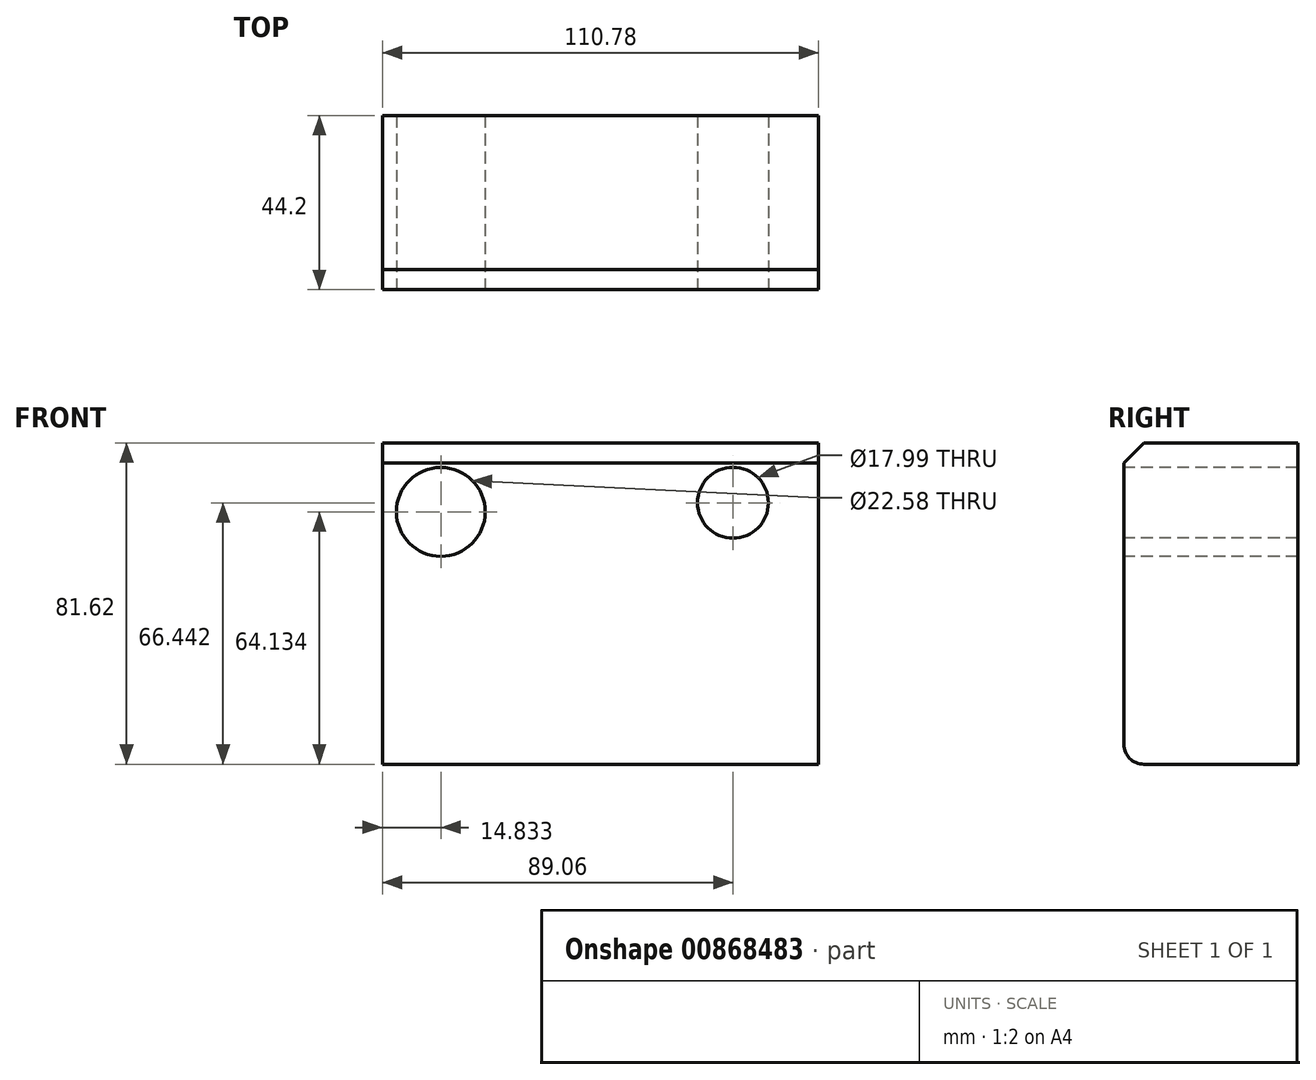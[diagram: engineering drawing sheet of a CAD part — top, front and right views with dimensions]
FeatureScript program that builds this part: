
annotation { "Feature Type Name" : "Feature", "Feature Type Description" : "" }
export const myFeature = defineFeature(function(context is Context, id is Id, definition is map)
    precondition{}
    {
        {
            var Q0;
            Q0=qCreatedBy(makeId("Front.planeOp"),FACE);
            var sketch = newSketch(context, id + "F0", { "sketchPlane" : qUnion([Q0])});
            skLineSegment(sketch, "E0.bottom", {"start": v(55.39, -40.8) * mm, "end": v(-55.39, -40.8) * mm});
            skLineSegment(sketch, "E0.top", {"start": v(55.39, 40.8) * mm, "end": v(-55.39, 40.8) * mm});
            skLineSegment(sketch, "E0.left", {"start": v(55.39, -40.8) * mm, "end": v(55.39, 40.8) * mm});
            skLineSegment(sketch, "E0.right", {"start": v(-55.39, -40.8) * mm, "end": v(-55.39, 40.8) * mm});
            skPoint(sketch, "E0.middle", {"position": v(0, 0) * mm});
            skSolve(sketch);
        }
        {
            var Q0;
            Q0=makeQuery(id+"F0.imprint","IMPRINT",FACE,{"disambiguationData":[TD([[makeQuery(id+"F0.imprint","IMPRINT",EDGE,{"derivedFrom":sQuery(id+"F0.wireOp",EDGE,"E0.bottom")}),-1.0]])]});
            extrude(context, id + "F1", {"entities" : qUnion([Q0]), "depth" : 44.2 * mm, "offsetDistance" : 25.4 * mm});
        }
        {
            var Q0;
            Q0=makeQuery(id+"F1.opExtrude","CAP_FACE",FACE,{"disambiguationData":[OSD([sQuery(id+"F0.wireOp",EDGE,"E0.bottom"),sQuery(id+"F0.wireOp",EDGE,"E0.top"),sQuery(id+"F0.wireOp",EDGE,"E0.left"),sQuery(id+"F0.wireOp",EDGE,"E0.right")])],"isStart":false});
            var sketch = newSketch(context, id + "F2", { "sketchPlane" : qUnion([Q0])});
            skCircle(sketch, "E1", {"center": v(-40.56, 23.32) * mm, "radius": 11.3 * mm});
            skCircle(sketch, "E2", {"center": v(33.67, 25.63) * mm, "radius": 9 * mm});
            skSolve(sketch);
        }
        {
            var Q0;
            Q0 = qSketchRegion(id + "F2", true);
            extrude(context, id + "F3", {"entities" : qUnion([Q0]), "operationType" : NewBodyOperationType.REMOVE, "endBound" : BoundingType.UP_TO_NEXT, "oppositeDirection" : true, "depth" : 25.4 * mm, "offsetDistance" : 25.4 * mm});
        }
        {
            var Q0;
            Q0=makeQuery(id+"F1.opExtrude","CAP_EDGE",EDGE,{"disambiguationData":[OSD([sQuery(id+"F0.wireOp",EDGE,"E0.top")])],"isStart":false});
            chamfer(context, id + "F4", {"entities" : qUnion([Q0]), "width" : 5.08 * mm, "tangentPropagation" : true});
        }
        {
            var Q0;
            Q0=makeQuery(id+"F1.opExtrude","CAP_EDGE",EDGE,{"disambiguationData":[OSD([sQuery(id+"F0.wireOp",EDGE,"E0.bottom")])],"isStart":false});
            fillet(context, id + "F5", {"entities" : qUnion([Q0]), "radius" : 5.08 * mm, "tangentPropagation" : true, "allowEdgeOverflow" : false});
        }
    });
